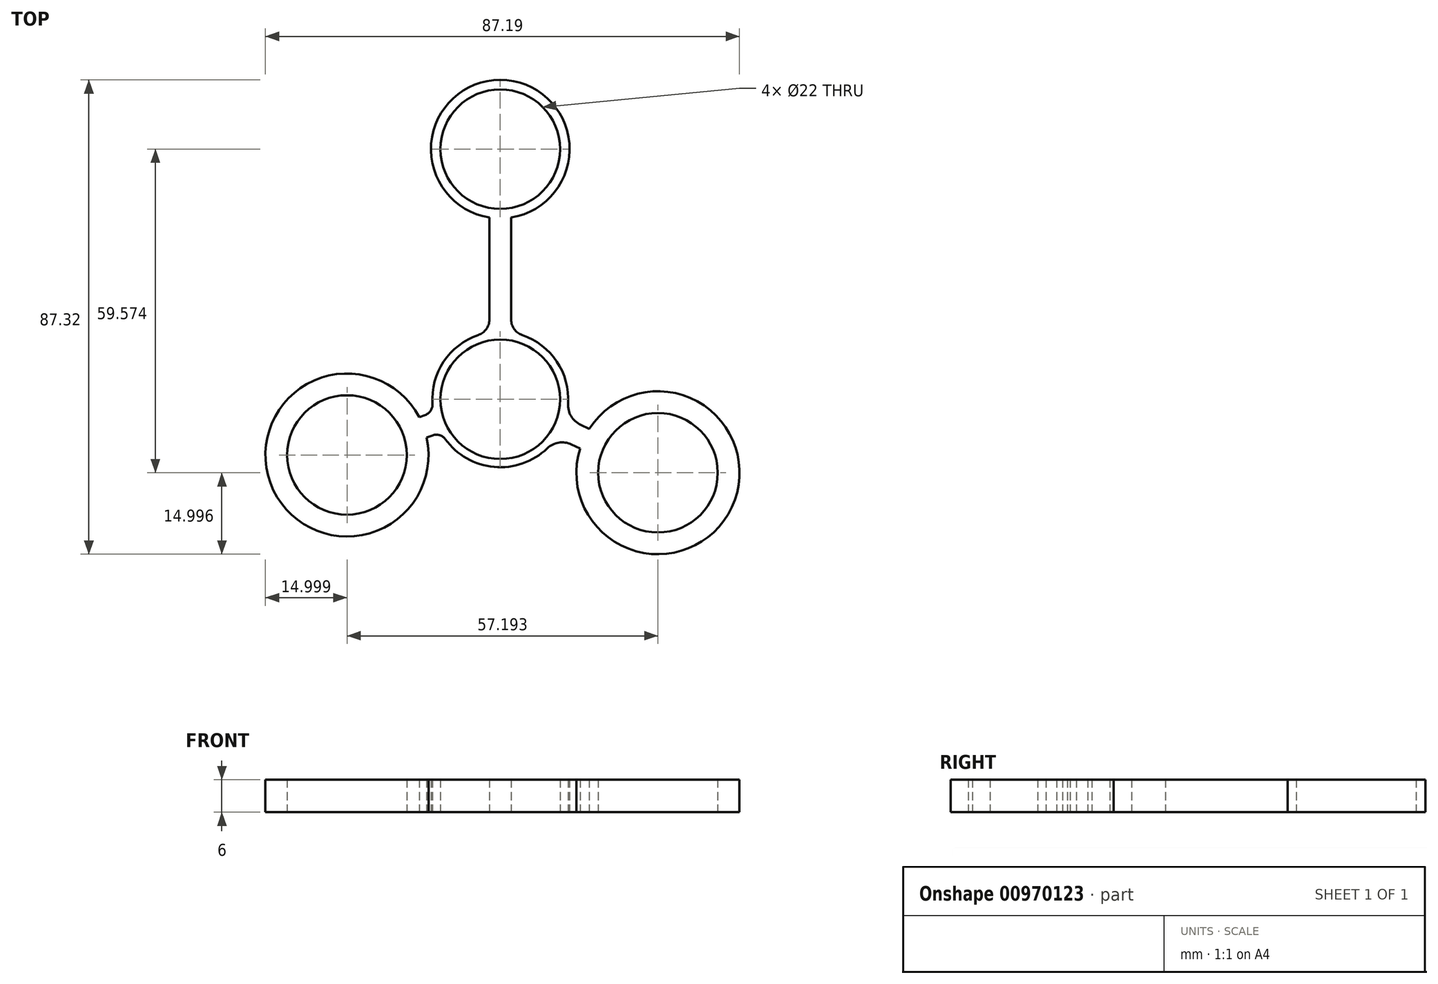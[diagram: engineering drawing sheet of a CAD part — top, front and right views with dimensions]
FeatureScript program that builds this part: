
annotation { "Feature Type Name" : "Feature", "Feature Type Description" : "" }
export const myFeature = defineFeature(function(context is Context, id is Id, definition is map)
    precondition{}
    {
        {
            var Q0;
            Q0=qCreatedBy(makeId("Top.planeOp"),FACE);
            var sketch = newSketch(context, id + "F0", { "sketchPlane" : qUnion([Q0])});
            skArc(sketch, "E0", {"start": v(-4.03, 11.83) * mm, "mid": v(-10.41, 6.92) * mm, "end": v(-12.47, -0.87) * mm});
            skCircle(sketch, "E1", {"center": v(0, 0) * mm, "radius": 11 * mm});
            skArc(sketch, "E2", {"start": v(2, 33.46) * mm, "mid": v(0, 58.8) * mm, "end": v(-2, 33.46) * mm});
            skCircle(sketch, "E3", {"center": v(0, 46.05) * mm, "radius": 11 * mm});
            skLineSegment(sketch, "E4", {"start": v(2, 33.46) * mm, "end": v(2, 14.67) * mm});
            skLineSegment(sketch, "E5", {"start": v(-2, 33.46) * mm, "end": v(-2, 14.67) * mm});
            skArc(sketch, "E6", {"start": v(14.68, -9.05) * mm, "mid": v(42.6, -19.86) * mm, "end": v(16.37, -5.43) * mm});
            skCircle(sketch, "E7", {"center": v(29, -13.52) * mm, "radius": 11 * mm});
            skPoint(sketch, "E8.visualSharp", {"position": v(-2, 12.34) * mm});
            skArc(sketch, "E8.filletArc", {"start": v(-4.03, 11.83) * mm, "mid": v(-2.56, 12.93) * mm, "end": v(-2, 14.67) * mm});
            skPoint(sketch, "E9.visualSharp", {"position": v(2, 12.34) * mm});
            skArc(sketch, "E9.filletArc", {"start": v(2, 14.67) * mm, "mid": v(2.56, 12.93) * mm, "end": v(4.03, 11.83) * mm});
            skLineSegment(sketch, "E10.trimOffspring", {"start": v(14.78, -4.68) * mm, "end": v(16.37, -5.43) * mm});
            skLineSegment(sketch, "E11.trimOffspring", {"start": v(13.09, -8.3) * mm, "end": v(14.68, -9.05) * mm});
            skArc(sketch, "E12.trimOffspring", {"start": v(12.47, -0.8) * mm, "mid": v(10.4, 6.95) * mm, "end": v(4.03, 11.83) * mm});
            skArc(sketch, "E13.MirrorCS", {"start": v(-13.54, -7.06) * mm, "mid": v(-42.29, -15.4) * mm, "end": v(-14.9, -3.3) * mm});
            skLineSegment(sketch, "E14.MirrorCS", {"start": v(-13.78, -2.89) * mm, "end": v(-14.9, -3.3) * mm});
            skLineSegment(sketch, "E15.MirrorCS", {"start": v(-12.41, -6.65) * mm, "end": v(-13.54, -7.06) * mm});
            skCircle(sketch, "E16", {"center": v(-28.2, -10.26) * mm, "radius": 11 * mm});
            skArc(sketch, "E17.trimOffspring", {"start": v(-10.11, -7.35) * mm, "mid": v(-1.12, -12.45) * mm, "end": v(8.63, -9.04) * mm});
            skPoint(sketch, "E18.visualSharp", {"position": v(-12.28, -2.34) * mm});
            skArc(sketch, "E18.filletArc", {"start": v(-13.78, -2.89) * mm, "mid": v(-12.79, -2.1) * mm, "end": v(-12.47, -0.87) * mm});
            skPoint(sketch, "E19.visualSharp", {"position": v(12.03, -3.4) * mm});
            skArc(sketch, "E19.filletArc", {"start": v(12.47, -0.8) * mm, "mid": v(13.03, -3.1) * mm, "end": v(14.78, -4.68) * mm});
            skPoint(sketch, "E20.visualSharp", {"position": v(10.34, -7.03) * mm});
            skArc(sketch, "E20.filletArc", {"start": v(13.09, -8.3) * mm, "mid": v(10.75, -7.99) * mm, "end": v(8.63, -9.04) * mm});
            skLineSegment(sketch, "E21", {"start": v(0, 0) * mm, "end": v(-28.2, -10.26) * mm, "construction": true});
            skLineSegment(sketch, "E22", {"start": v(0, 0) * mm, "end": v(29, -13.52) * mm, "construction": true});
            skPoint(sketch, "E23.visualSharp", {"position": v(-10.91, -6.1) * mm});
            skArc(sketch, "E23.filletArc", {"start": v(-10.11, -7.35) * mm, "mid": v(-11.14, -6.61) * mm, "end": v(-12.41, -6.65) * mm});
            skSolve(sketch);
        }
        {
            var Q0;
            Q0=makeQuery(id+"F0.imprint","IMPRINT",FACE,{"disambiguationData":[TD([[makeQuery(id+"F0.imprint","IMPRINT",EDGE,{"derivedFrom":sQuery(id+"F0.wireOp",EDGE,"E0")}),1.0]])]});
            extrude(context, id + "F1", {"entities" : qUnion([Q0]), "endBound" : BoundingType.SYMMETRIC, "depth" : 6 * mm, "offsetDistance" : 25 * mm});
        }
    });
